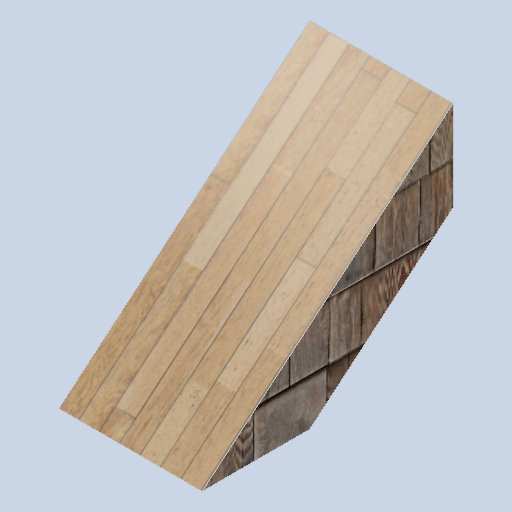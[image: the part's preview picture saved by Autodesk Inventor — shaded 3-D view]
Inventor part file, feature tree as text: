
AUTODESK INVENTOR PART (.ipt)
format: ipt  version: 2024.2 (Build 282272000, 272)  size: 304,640 bytes
history: native  units: in
note: dims shown in document units (in); Inventor stores cm internally (conversion verified against a paired STEP export)
features: other x3, sketch x1
ambient origin geometry x8: Origin, YZ Plane, XZ Plane, XY Plane, X Axis, Y Axis, Z Axis, Center Point
bodies: Body1 (feature_tree)
feature tree (4):
  other  "frame_rib_01.ipt"
  other  "Solid3::frame_rib_01.ipt"
  other  "TaggingFeature1"
  sketch  "Sketch1"  dims[d0=0.3937in]
